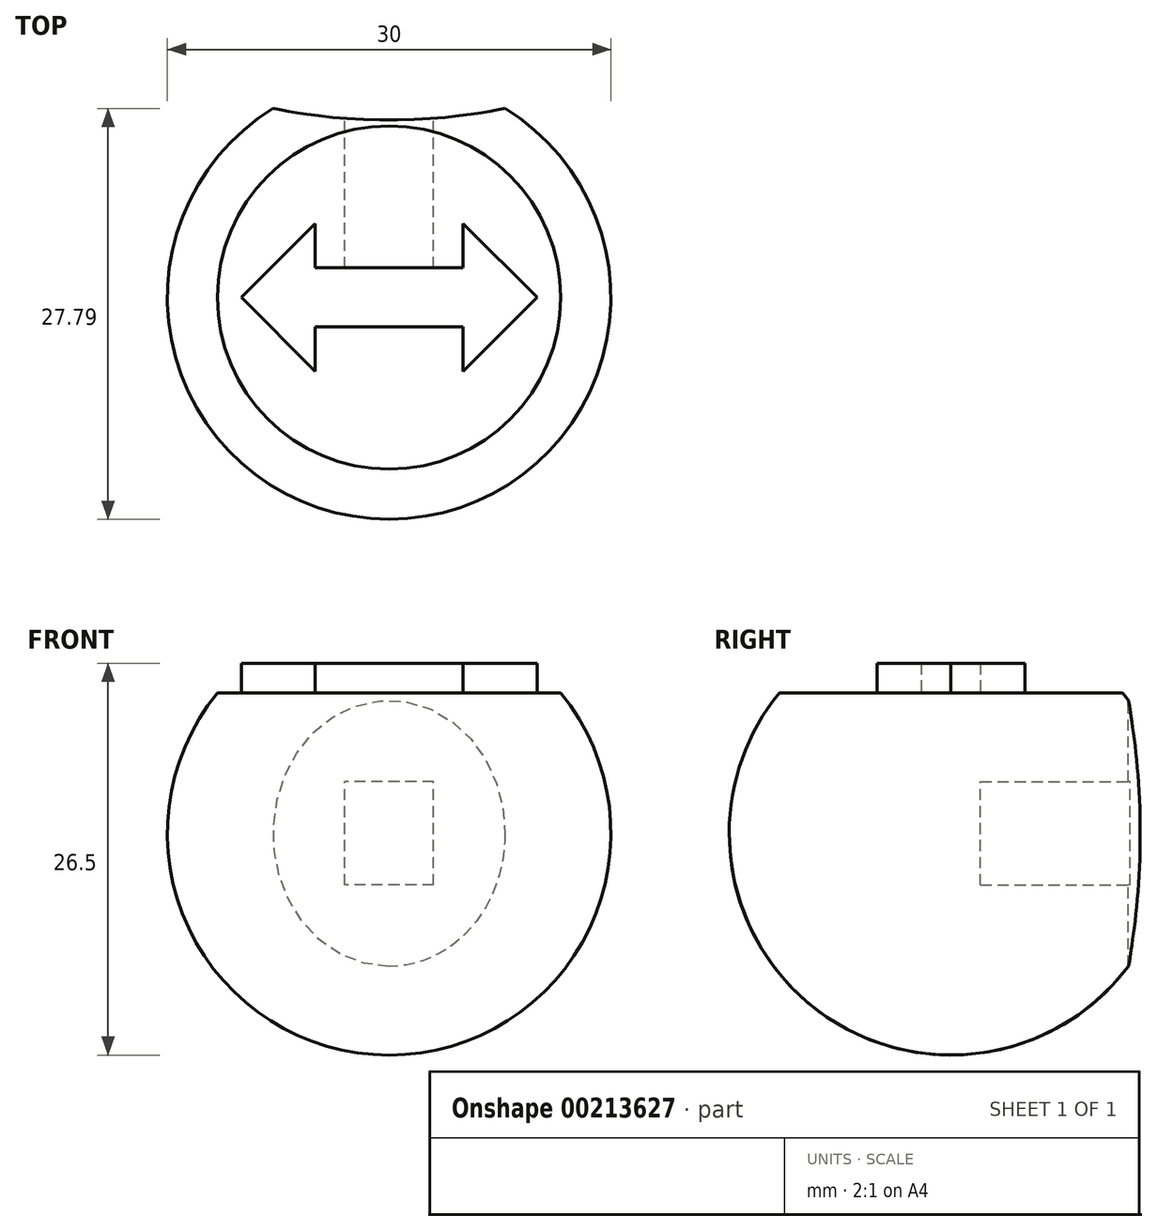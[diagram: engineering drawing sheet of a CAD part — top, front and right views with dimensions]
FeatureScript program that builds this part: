
annotation { "Feature Type Name" : "Feature", "Feature Type Description" : "" }
export const myFeature = defineFeature(function(context is Context, id is Id, definition is map)
    precondition{}
    {
        {
            var Q0;
            Q0=qCreatedBy(makeId("Right.planeOp"),FACE);
            var sketch = newSketch(context, id + "F0", { "sketchPlane" : qUnion([Q0])});
            skLineSegment(sketch, "E0", {"start": v(0, 0) * mm, "end": v(-30, 0) * mm});
            skArc(sketch, "E1", {"start": v(0, 0) * mm, "mid": v(-15, 15) * mm, "end": v(-30, 0) * mm});
            skSolve(sketch);
        }
        {
            var Q0;
            Q0=qSketchRegion(id+"F0",true);
            var Q1;
            Q1=sQuery(id+"F0.wireOp",EDGE,"E0");
            revolve(context, id + "F1", {"entities" : qUnion([Q0]), "axis" : qUnion([Q1]), "revolveType" : RevolveType.FULL});
        }
        {
            var Q0;
            Q0=qCreatedBy(makeId("Top.planeOp"),FACE);
            cPlane(context, id + "F2", {"entities" : qUnion([Q0]), "cplaneType" : CPlaneType.OFFSET, "offset" : 15 * mm, "width" : 150 * mm, "height" : 150 * mm});
        }
        {
            var Q0;
            Q0=qCreatedBy(id+"F2.planeOp",FACE);
            var sketch = newSketch(context, id + "F3", { "sketchPlane" : qUnion([Q0])});
            skLineSegment(sketch, "E2", {"start": v(0, 0) * mm, "end": v(0, -16.03) * mm, "construction": true});
            skLineSegment(sketch, "E3", {"start": v(0, 0) * mm, "end": v(-15, 0) * mm});
            skLineSegment(sketch, "E4", {"start": v(0, 0) * mm, "end": v(15, 0) * mm});
            skArc(sketch, "E5", {"start": v(-15, 0) * mm, "mid": v(0, -3) * mm, "end": v(15, 0) * mm});
            skSolve(sketch);
        }
        {
            var Q0;
            Q0=qSketchRegion(id+"F3",true);
            extrude(context, id + "F4", {"entities" : qUnion([Q0]), "operationType" : NewBodyOperationType.REMOVE, "endBound" : BoundingType.THROUGH_ALL, "oppositeDirection" : true, "depth" : 25 * mm});
        }
        {
            var Q0;
            Q0=qCreatedBy(makeId("Front.planeOp"),FACE);
            var sketch = newSketch(context, id + "F5", { "sketchPlane" : qUnion([Q0])});
            skLineSegment(sketch, "E6.bottom", {"start": v(3, -3.5) * mm, "end": v(-3, -3.5) * mm});
            skLineSegment(sketch, "E6.top", {"start": v(3, 3.5) * mm, "end": v(-3, 3.5) * mm});
            skLineSegment(sketch, "E6.left", {"start": v(3, -3.5) * mm, "end": v(3, 3.5) * mm});
            skLineSegment(sketch, "E6.right", {"start": v(-3, -3.5) * mm, "end": v(-3, 3.5) * mm});
            skPoint(sketch, "E6.middle", {"position": v(0, 0) * mm});
            skSolve(sketch);
        }
        {
            var Q0;
            Q0=qSketchRegion(id+"F5",true);
            extrude(context, id + "F6", {"entities" : qUnion([Q0]), "operationType" : NewBodyOperationType.REMOVE, "depth" : 13 * mm});
        }
        {
            var Q0;
            Q0=qCreatedBy(makeId("Front.planeOp"),FACE);
            var sketch = newSketch(context, id + "F7", { "sketchPlane" : qUnion([Q0])});
            skLineSegment(sketch, "E7", {"start": v(23.47, 9.5) * mm, "end": v(-26.93, 9.5) * mm});
            skLineSegment(sketch, "E8", {"start": v(23.47, 9.5) * mm, "end": v(23.47, 17.53) * mm});
            skLineSegment(sketch, "E9", {"start": v(23.47, 17.53) * mm, "end": v(-26.93, 17.53) * mm});
            skLineSegment(sketch, "E10", {"start": v(-26.93, 17.53) * mm, "end": v(-26.93, 9.5) * mm});
            skSolve(sketch);
        }
        {
            var Q0;
            Q0 = qSketchRegion(id + "F7", true);
            extrude(context, id + "F8", {"entities" : qUnion([Q0]), "operationType" : NewBodyOperationType.REMOVE, "endBound" : BoundingType.THROUGH_ALL, "depth" : 25 * mm});
        }
        {
            var Q0;
            Q0=makeQuery(id+"F8.boolean.opBoolean","COPY",FACE,{"derivedFrom":makeQuery(id+"F8.opExtrude","SWEPT_FACE",FACE,{"disambiguationData":[OSD([sQuery(id+"F7.wireOp",EDGE,"E7")])]})});
            var sketch = newSketch(context, id + "F9", { "sketchPlane" : qUnion([Q0])});
            skLineSegment(sketch, "E11", {"start": v(0, -15) * mm, "end": v(-11.6, -15) * mm, "construction": true});
            skLineSegment(sketch, "E12", {"start": v(0, -15) * mm, "end": v(11.6, -15) * mm, "construction": true});
            skLineSegment(sketch, "E13.bottom", {"start": v(-5, -13) * mm, "end": v(5, -13) * mm});
            skLineSegment(sketch, "E13.top", {"start": v(-5, -17) * mm, "end": v(5, -17) * mm});
            skLineSegment(sketch, "E13.left", {"start": v(-5, -13) * mm, "end": v(-5, -17) * mm});
            skLineSegment(sketch, "E13.right", {"start": v(5, -13) * mm, "end": v(5, -17) * mm});
            skPoint(sketch, "E13.middle", {"position": v(0, -15) * mm});
            skLineSegment(sketch, "E14", {"start": v(5, -13) * mm, "end": v(5, -10) * mm});
            skLineSegment(sketch, "E15", {"start": v(5, -10) * mm, "end": v(10, -15) * mm});
            skLineSegment(sketch, "E16", {"start": v(10, -15) * mm, "end": v(5, -20) * mm});
            skLineSegment(sketch, "E17", {"start": v(5, -20) * mm, "end": v(5, -17) * mm});
            skLineSegment(sketch, "E18", {"start": v(0, -17) * mm, "end": v(0, -13) * mm, "construction": true});
            skLineSegment(sketch, "E19.MirrorCS", {"start": v(-5, -13) * mm, "end": v(-5, -10) * mm});
            skLineSegment(sketch, "E20.MirrorCS", {"start": v(-5, -10) * mm, "end": v(-10, -15) * mm});
            skLineSegment(sketch, "E21.MirrorCS", {"start": v(-10, -15) * mm, "end": v(-5, -20) * mm});
            skLineSegment(sketch, "E22.MirrorCS", {"start": v(-5, -20) * mm, "end": v(-5, -17) * mm});
            skSolve(sketch);
        }
        {
            var Q0;
            Q0 = qSketchRegion(id + "F9", true);
            extrude(context, id + "F10", {"entities" : qUnion([Q0]), "operationType" : NewBodyOperationType.ADD, "depth" : 2 * mm});
        }
    });
